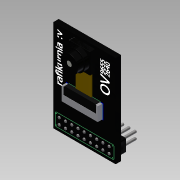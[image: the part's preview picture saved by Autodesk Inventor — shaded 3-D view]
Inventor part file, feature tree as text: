
AUTODESK INVENTOR PART (.ipt)
format: ipt  version: 2015 SP1 (Build 190203100, 203)  size: 400,896 bytes
history: native  units: mm
features: extrude x12, sketch x6, projected_geometry x4, fillet x3
ambient origin geometry x8: Origin, YZ Plane, XZ Plane, XY Plane, X Axis, Y Axis, Z Axis, Center Point
bodies: Solid1 (feature_tree)
feature tree (25):
  sketch  "Sketch1"  dims[d0=24.32mm d1=35.9mm]
  extrude  "Extrusion1"  Depth=35.9mm
  extrude  "Extrusion2"  Depth=8.05mm
  extrude  "Extrusion3"  Depth=1.0mm
  extrude  "Extrusion4"  Depth=7.88mm
  extrude  "Extrusion5"  Depth=6.05mm
  extrude  "Extrusion6"  Depth=0.25mm
  extrude  "Extrusion7"  Depth=1.0mm
  extrude  "Extrusion8"  TaperAngle=90.0deg  [1 undecoded]
  extrude  "Extrusion9"  Depth=0.25mm
  extrude  "Extrusion10"  Depth=1.0mm
  fillet  "Fillet1"  [1 undecoded]
  fillet  "Fillet2"  Radius=5.33mm
  fillet  "Fillet3"  Radius=2.432mm
  extrude  "Extrusion11"  Depth=0.1mm
  extrude  "Extrusion12"  Depth=1.0mm
  sketch  "Sketch4"  dims[d6=8.05mm d7=7.88mm]
  sketch  "Sketch5"  dims[d8=6.84mm d9=6.05mm]
  sketch  "Sketch6"  dims[d10=8.63mm d13=0.25mm d14=1.0mm d15=90.0deg d16=0.25mm d17=1.0mm d18=90.0deg d19=5.33mm d21=2.432mm d22=2.432mm d23=1.0mm d24=90.0mm d26=2.432mm d27=20.0mm d29=2.432mm d32=22.96mm d33=4.98mm d34=2.09mm d35=0.0mm d36=4.05mm d37=0.0mm d38=5.81mm d39=0.0mm d40=8.1mm d41=0.0mm d42=2.5mm d43=0.0mm d44=3.88mm d45=0.0mm d46=2.09mm d47=0.0mm d48=2.62mm d49=0.0mm d50=8.2mm d51=0.0mm d52=2.5mm d53=0.0mm d54=0.25mm d55=0.5mm d56=0.125mm d60=0.7mm d61=0.7mm d62=2.41mm d63=0.1mm d64=0.0mm d65=2.0mm d66=0.1mm d67=0.0mm d68=0.1mm]
  sketch  "Sketch2"  dims[d2=8.22mm d3=8.05mm]
  sketch  "Sketch3"  dims[d4=1.0mm d5=8.05mm]
  projected_geometry  "Projected Loop2"
  projected_geometry  "Projected Loop3"
  projected_geometry  "Projected Loop4"
  projected_geometry  "Projected Loop5"
note: 2 required parameter values undecoded (feature->parameter linkage not recoverable at this tier; creation-order binding heuristic only, values carry confidence <= 0.55)
